# Revit family: Термостатический клапан HERZ-TS-98-VH М 30х1,5 с плавной, открытой преднастройкой, угловой, осевой специальный 7628
name_source: partatom
category: Rohrzubehör
units: mm (PartAtom-declared; Revit-internal decimal feet)

## family parameters
Arbeitsebenenbasiert = Nein
Beim Laden mit Abzugskörper schneiden = Nein
Bemaßung runder Anschluss = Durchmesser verwenden
Gemeinsam genutzt = Nein
Immer vertikal = Ja
OmniClass-Nummer = 23.65.55.14
OmniClass-Titel = Valves for Liquid Services
Teiletyp = Unterbricht

## types (1)
- Термостатический клапан HERZ-TS-98-VH М 30х1,5 с плавной, открытой преднастройкой, угловой, осевой специальный 7628
    D01 = 15 mm  [stored 0.0492126 ft]
    D02 = 10.5 mm  [stored 0.0344488 ft]
    D03 = 11.5 mm  [stored 0.0377297 ft]
    D04 = 9.525 mm  [stored 0.03125 ft]
    D05 = 15 mm  [stored 0.0492126 ft]
    D06 = 10.65 mm  [stored 0.0349409 ft]
    D07 = 17.1 mm
    D08 = 5.3 mm
    G1 = 7.5 mm  [stored 0.0246063 ft]
    G2 = 7.5 mm  [stored 0.0246063 ft]
    GT = 9.5 mm
    H01 = 33.5 mm
    H02 = 22.35 mm  [stored 0.0733268 ft]
    H03 = 4.4 mm
    H04 = 12.9 mm
    Hersteller = HERZ Armaturen Ges.m.b.H.
    L01 = 31.5 mm  [stored 0.103346 ft]
    L02 = 27 mm  [stored 0.0885827 ft]
    L03 = 7.5 mm  [stored 0.0246063 ft]
    L04 = 28 mm
    L05 = 3.5 mm  [stored 0.0114829 ft]
    L06 = 14 mm  [stored 0.0459318 ft]
    L07 = 20.3 mm
    L08 = 13.2 mm
    L09 = 19.5 mm  [stored 0.0639764 ft]
    L10 = 7.5 mm  [stored 0.0246063 ft]
    L11 = 28 mm
    LO1 = 16 mm  [stored 0.0524934 ft]
    Nennweite = 15 mm  [stored 0.0492126 ft]
    R01 = 7 mm  [stored 0.0229659 ft]
    R02 = 6.75 mm  [stored 0.0221457 ft]
    R03 = 9 mm  [stored 0.0295276 ft]
    R04 = 11.5 mm  [stored 0.0377297 ft]
    R05 = 13.5 mm  [stored 0.0442913 ft]
    R06 = 4 mm  [stored 0.0131234 ft]
    S01 = 10 mm  [stored 0.0328084 ft]
    S02 = 26.8 mm  [stored 0.0879265 ft]
    SCRNCODE = 05;00;02
    SCRNSEQ = ARM;ARM_TYP="ALLF";2
    URL = www.herz-armaturen.ru
    Защитный колпачок = Пластик, светло-серый
    Исполнение = Все модели поставляются в никелированном исполнении со светло-серым защитным колпачком.
    Корпус = Никелированная латунь
    Макс. рабочая температура = 120 °C
    Макс. рабочее давление = 1000000.0 Pa
    Номер заказа = 1762826
    Область применения = Системы водяного отопления, в которых гидравлическая балансировка с помощью запорных клапанов для отключения радиаторов невозможна или нежелательна.
    Соединительная резьба для термостатической головки = M30x1.5
    Среда = Качество воды в соответствии с ÖNORM H 5195 или директивой VDI 2035.

note: [stored X ft] marks values corroborated as IEEE doubles in the binary element streams (Revit-internal decimal feet)
